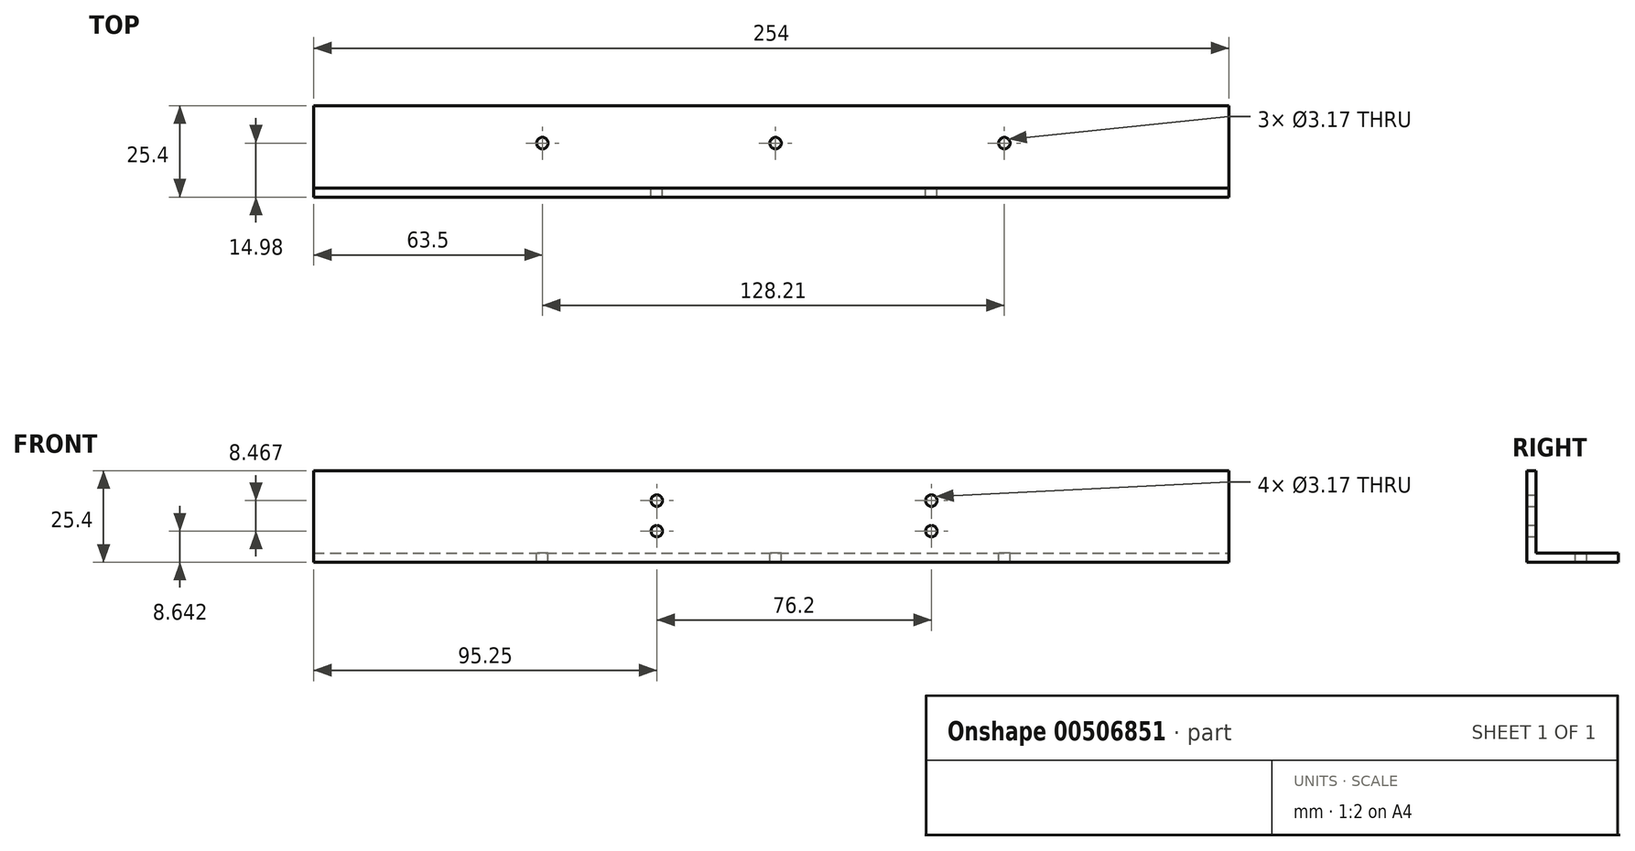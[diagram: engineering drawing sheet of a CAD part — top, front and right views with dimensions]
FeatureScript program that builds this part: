
annotation { "Feature Type Name" : "Feature", "Feature Type Description" : "" }
export const myFeature = defineFeature(function(context is Context, id is Id, definition is map)
    precondition{}
    {
        {
            var Q0;
            Q0=qCreatedBy(makeId("Top.planeOp"),FACE);
            var sketch = newSketch(context, id + "F0", { "sketchPlane" : qUnion([Q0])});
            skLineSegment(sketch, "E0.bottom", {"start": v(-128.2, 17.21) * mm, "end": v(125.8, 17.21) * mm});
            skLineSegment(sketch, "E0.top", {"start": v(-128.2, -8.19) * mm, "end": v(125.8, -8.19) * mm});
            skLineSegment(sketch, "E0.left", {"start": v(-128.2, 17.21) * mm, "end": v(-128.2, -8.19) * mm});
            skLineSegment(sketch, "E0.right", {"start": v(125.8, 17.21) * mm, "end": v(125.8, -8.19) * mm});
            skSolve(sketch);
        }
        {
            var Q0;
            Q0=makeQuery(id+"F0.imprint","IMPRINT",FACE,{"disambiguationData":[TD([[makeQuery(id+"F0.imprint","IMPRINT",EDGE,{"derivedFrom":sQuery(id+"F0.wireOp",EDGE,"E0.bottom")}),-1.0]])]});
            extrude(context, id + "F1", {"entities" : qUnion([Q0]), "depth" : 25.4 * mm, "offsetDistance" : 25.4 * mm});
        }
        {
            var Q0;
            Q0=makeQuery(id+"F1.opExtrude","CAP_FACE",FACE,{"disambiguationData":[OSD([sQuery(id+"F0.wireOp",EDGE,"E0.bottom"),sQuery(id+"F0.wireOp",EDGE,"E0.top"),sQuery(id+"F0.wireOp",EDGE,"E0.left"),sQuery(id+"F0.wireOp",EDGE,"E0.right")])],"isStart":false});
            var Q1;
            Q1=makeQuery(id+"F1.opExtrude","SWEPT_FACE",FACE,{"disambiguationData":[OSD([sQuery(id+"F0.wireOp",EDGE,"E0.bottom")])]});
            var Q2;
            Q2=makeQuery(id+"F1.opExtrude","SWEPT_FACE",FACE,{"disambiguationData":[OSD([sQuery(id+"F0.wireOp",EDGE,"E0.right")])]});
            var Q3;
            Q3=makeQuery(id+"F1.opExtrude","SWEPT_FACE",FACE,{"disambiguationData":[OSD([sQuery(id+"F0.wireOp",EDGE,"E0.left")])]});
            shell(context, id + "F2", {"entities" : qUnion([Q0, Q1, Q2, Q3]), "thickness" : 2.54 * mm});
        }
        {
            var Q0;
            Q0=makeQuery(id+"F2.opShell","OFFSET_FACE",FACE,{"disambiguationData":[OSD([sQuery(id+"F0.wireOp",EDGE,"E0.bottom"),sQuery(id+"F0.wireOp",EDGE,"E0.top"),sQuery(id+"F0.wireOp",EDGE,"E0.left"),sQuery(id+"F0.wireOp",EDGE,"E0.right")])]});
            var sketch = newSketch(context, id + "F3", { "sketchPlane" : qUnion([Q0])});
            skPoint(sketch, "E1", {"position": v(63.5, 6.79) * mm});
            skPoint(sketch, "E2", {"position": v(0, 6.79) * mm});
            skPoint(sketch, "E3", {"position": v(-64.7, 6.79) * mm});
            skSolve(sketch);
        }
        {
            var Q0;
            Q0=sQuery(id+"F3.wireOp",VERTEX,"E1");
            var Q1;
            Q1=sQuery(id+"F3.wireOp",VERTEX,"E2");
            var Q2;
            Q2=sQuery(id+"F3.wireOp",VERTEX,"E3");
            var Q3;
            Q3=makeQuery(id+"F1.opExtrude","SWEPT_BODY",BODY,{"disambiguationData":[OSD([sQuery(id+"F0.wireOp",EDGE,"E0.bottom"),sQuery(id+"F0.wireOp",EDGE,"E0.top"),sQuery(id+"F0.wireOp",EDGE,"E0.left"),sQuery(id+"F0.wireOp",EDGE,"E0.right")])]});
            hole(context, id + "F4", {"style" : HoleStyle.SIMPLE, "endStyle" : HoleEndStyle.THROUGH, "holeDiameter" : 3.17 * mm, "majorDiameter" : 6.35 * mm, "isTappedThrough" : true, "tappedDepth" : 12.7 * mm, "tapClearance" : 3, "locations" : qUnion([Q0, Q1, Q2]), "scope" : qUnion([Q3])});
        }
        {
            var Q0;
            Q0=makeQuery(id+"F2.opShell","OFFSET_FACE",FACE,{"disambiguationData":[OSD([sQuery(id+"F0.wireOp",EDGE,"E0.top")])]});
            var sketch = newSketch(context, id + "F5", { "sketchPlane" : qUnion([Q0])});
            skPoint(sketch, "E4", {"position": v(-43.24, 17.1) * mm});
            skPoint(sketch, "E5", {"position": v(-43.24, 8.64) * mm});
            skPoint(sketch, "E6", {"position": v(32.96, 17.1) * mm});
            skPoint(sketch, "E7", {"position": v(32.96, 8.64) * mm});
            skSolve(sketch);
        }
        {
            var Q0;
            Q0=sQuery(id+"F5.wireOp",VERTEX,"E5");
            var Q1;
            Q1=sQuery(id+"F5.wireOp",VERTEX,"E4");
            var Q2;
            Q2=sQuery(id+"F5.wireOp",VERTEX,"E6");
            var Q3;
            Q3=sQuery(id+"F5.wireOp",VERTEX,"E7");
            var Q4;
            Q4=makeQuery(id+"F1.opExtrude","SWEPT_BODY",BODY,{"disambiguationData":[OSD([sQuery(id+"F0.wireOp",EDGE,"E0.bottom"),sQuery(id+"F0.wireOp",EDGE,"E0.top"),sQuery(id+"F0.wireOp",EDGE,"E0.left"),sQuery(id+"F0.wireOp",EDGE,"E0.right")])]});
            hole(context, id + "F6", {"style" : HoleStyle.SIMPLE, "endStyle" : HoleEndStyle.THROUGH, "holeDiameter" : 3.17 * mm, "majorDiameter" : 6.35 * mm, "isTappedThrough" : true, "tappedDepth" : 12.7 * mm, "tapClearance" : 3, "locations" : qUnion([Q0, Q1, Q2, Q3]), "scope" : qUnion([Q4])});
        }
    });
